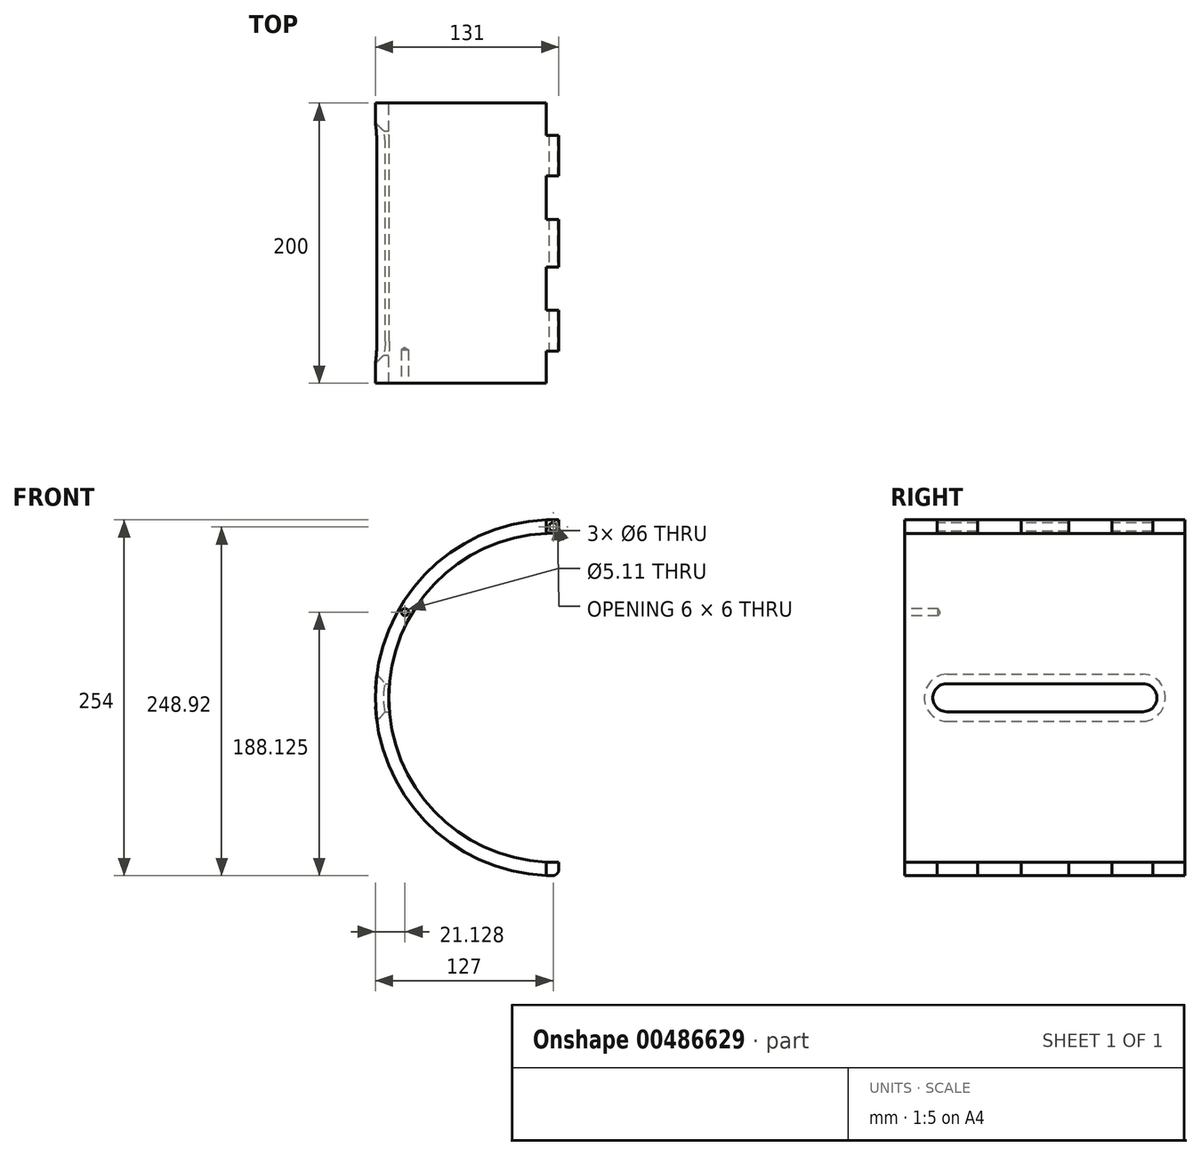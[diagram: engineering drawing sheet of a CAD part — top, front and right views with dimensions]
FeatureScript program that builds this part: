
annotation { "Feature Type Name" : "Feature", "Feature Type Description" : "" }
export const myFeature = defineFeature(function(context is Context, id is Id, definition is map)
    precondition{}
    {
        {
            var Q0;
            Q0=qCreatedBy(makeId("Front.planeOp"),FACE);
            var sketch = newSketch(context, id + "F0", { "sketchPlane" : qUnion([Q0])});
            skCircle(sketch, "E0", {"center": v(0, 0) * mm, "radius": 117.42 * mm});
            skCircle(sketch, "E1", {"center": v(0, 0) * mm, "radius": 127 * mm});
            skSolve(sketch);
        }
        {
            var Q0;
            Q0=makeQuery(id+"F0.imprint","IMPRINT",FACE,{"disambiguationData":[TD([[makeQuery(id+"F0.imprint","IMPRINT",EDGE,{"derivedFrom":sQuery(id+"F0.wireOp",EDGE,"E0")}),-1.0]])]});
            extrude(context, id + "F1", {"entities" : qUnion([Q0]), "endBound" : BoundingType.SYMMETRIC, "depth" : 200 * mm});
        }
        {
            var Q0;
            Q0=qCreatedBy(makeId("Front.planeOp"),FACE);
            var sketch = newSketch(context, id + "F2", { "sketchPlane" : qUnion([Q0])});
            skLineSegment(sketch, "E2", {"start": v(0, 0) * mm, "end": v(0, 160.57) * mm, "construction": true});
            skSolve(sketch);
        }
        {
            var Q0;
            Q0=makeQuery(id+"F1.opExtrude","CAP_FACE",FACE,{"disambiguationData":[OSD([sQuery(id+"F0.wireOp",EDGE,"E0"),sQuery(id+"F0.wireOp",EDGE,"E1")])],"isStart":false});
            var sketch = newSketch(context, id + "F3", { "sketchPlane" : qUnion([Q0])});
            skCircle(sketch, "E3", {"center": v(0, 121.92) * mm, "radius": 3 * mm});
            skSolve(sketch);
        }
        {
            var Q0;
            Q0=makeQuery(id+"F3.imprint","IMPRINT",FACE,{"disambiguationData":[TD([[makeQuery(id+"F3.imprint","IMPRINT",EDGE,{"derivedFrom":sQuery(id+"F3.wireOp",EDGE,"E3")}),1.0]])]});
            extrude(context, id + "F4", {"entities" : qUnion([Q0]), "operationType" : NewBodyOperationType.REMOVE, "endBound" : BoundingType.THROUGH_ALL, "oppositeDirection" : true, "depth" : 25 * mm});
        }
        {
            var Q0;
            Q0=qCreatedBy(makeId("Top.planeOp"),FACE);
            var sketch = newSketch(context, id + "F5", { "sketchPlane" : qUnion([Q0])});
            skLineSegment(sketch, "E4", {"start": v(0, 100.89) * mm, "end": v(0, -112.88) * mm, "construction": true});
            skLineSegment(sketch, "E5", {"start": v(-85.43, 0) * mm, "end": v(71.36, 0) * mm, "construction": true});
            skLineSegment(sketch, "E6", {"start": v(4, 77) * mm, "end": v(4, 48) * mm});
            skLineSegment(sketch, "E7.0", {"start": v(-5, 104.48) * mm, "end": v(-5, 77) * mm});
            skLineSegment(sketch, "E8.0", {"start": v(-5, 48) * mm, "end": v(-5, 17) * mm});
            skLineSegment(sketch, "E9.0", {"start": v(4, 48) * mm, "end": v(-5, 48) * mm});
            skLineSegment(sketch, "E10", {"start": v(-5, 17) * mm, "end": v(4, 17) * mm});
            skPoint(sketch, "E11.orphan", {"position": v(-5, 17.5) * mm});
            skLineSegment(sketch, "E12.MirrorCS", {"start": v(-5, -17) * mm, "end": v(4, -17) * mm});
            skLineSegment(sketch, "E13.MirrorCS", {"start": v(4, -48) * mm, "end": v(-5, -48) * mm});
            skLineSegment(sketch, "E14.MirrorCS", {"start": v(-5, -48) * mm, "end": v(-5, -17) * mm});
            skLineSegment(sketch, "E15.MirrorCS", {"start": v(-5, -104.48) * mm, "end": v(-5, -77) * mm});
            skLineSegment(sketch, "E16.MirrorCS", {"start": v(-5, -77) * mm, "end": v(4, -77) * mm});
            skLineSegment(sketch, "E17.MirrorCS", {"start": v(4, -77) * mm, "end": v(4, -48) * mm});
            skLineSegment(sketch, "E18", {"start": v(-5, 77) * mm, "end": v(4, 77) * mm});
            skLineSegment(sketch, "E19", {"start": v(4, -17) * mm, "end": v(4, 17) * mm});
            skLineSegment(sketch, "E20", {"start": v(-5, -104.48) * mm, "end": v(139.16, -104.48) * mm});
            skLineSegment(sketch, "E21", {"start": v(139.16, -104.48) * mm, "end": v(139.16, 104.48) * mm});
            skLineSegment(sketch, "E22", {"start": v(139.16, 104.48) * mm, "end": v(-5, 104.48) * mm});
            skSolve(sketch);
        }
        {
            var Q0;
            Q0=makeQuery(id+"F5.imprint","IMPRINT",FACE,{"disambiguationData":[TD([[makeQuery(id+"F5.imprint","IMPRINT",EDGE,{"derivedFrom":sQuery(id+"F5.wireOp",EDGE,"E6")}),1.0]])]});
            extrude(context, id + "F6", {"entities" : qUnion([Q0]), "operationType" : NewBodyOperationType.REMOVE, "endBound" : BoundingType.SYMMETRIC, "oppositeDirection" : true, "depth" : 300 * mm});
        }
        {
            var Q0;
            Q0=makeQuery(id+"F6.boolean.opBoolean","INTERSECT",EDGE,{"disambiguationData":[OD(0.0)],"derivedFrom":[makeQuery(id+"F1.opExtrude","SWEPT_FACE",FACE,{"disambiguationData":[OSD([sQuery(id+"F0.wireOp",EDGE,"E1")])]}),makeQuery(id+"F6.opExtrude","SWEPT_FACE",FACE,{"disambiguationData":[OSD([sQuery(id+"F5.wireOp",EDGE,"E17.MirrorCS")])]})]});
            var Q1;
            Q1=makeQuery(id+"F6.boolean.opBoolean","INTERSECT",EDGE,{"disambiguationData":[OD(0.0)],"derivedFrom":[makeQuery(id+"F1.opExtrude","SWEPT_FACE",FACE,{"disambiguationData":[OSD([sQuery(id+"F0.wireOp",EDGE,"E1")])]}),makeQuery(id+"F6.opExtrude","SWEPT_FACE",FACE,{"disambiguationData":[OSD([sQuery(id+"F5.wireOp",EDGE,"E19")])]})]});
            var Q2;
            Q2=makeQuery(id+"F6.boolean.opBoolean","INTERSECT",EDGE,{"disambiguationData":[OD(0.0)],"derivedFrom":[makeQuery(id+"F1.opExtrude","SWEPT_FACE",FACE,{"disambiguationData":[OSD([sQuery(id+"F0.wireOp",EDGE,"E1")])]}),makeQuery(id+"F6.opExtrude","SWEPT_FACE",FACE,{"disambiguationData":[OSD([sQuery(id+"F5.wireOp",EDGE,"E6")])]})]});
            fillet(context, id + "F7", {"entities" : qUnion([Q0, Q1, Q2]), "radius" : 4.5 * mm, "tangentPropagation" : true, "allowEdgeOverflow" : false});
        }
        {
            var Q0;
            Q0=qCreatedBy(makeId("Right.planeOp"),FACE);
            var sketch = newSketch(context, id + "F8", { "sketchPlane" : qUnion([Q0])});
            skLineSegment(sketch, "E23", {"start": v(-123.75, 0) * mm, "end": v(112.08, 0) * mm, "construction": true});
            skArc(sketch, "E24", {"start": v(-70, 10) * mm, "mid": v(-80, 0) * mm, "end": v(-70, -10) * mm});
            skArc(sketch, "E25", {"start": v(70, -10) * mm, "mid": v(80, 0) * mm, "end": v(70, 10) * mm});
            skLineSegment(sketch, "E26", {"start": v(-70, 10) * mm, "end": v(70, 10) * mm});
            skLineSegment(sketch, "E27", {"start": v(-70, -10) * mm, "end": v(70, -10) * mm});
            skSolve(sketch);
        }
        {
            var Q0;
            Q0=makeQuery(id+"F8.imprint","IMPRINT",FACE,{"disambiguationData":[TD([[makeQuery(id+"F8.imprint","IMPRINT",EDGE,{"derivedFrom":sQuery(id+"F8.wireOp",EDGE,"E24")}),1.0]])]});
            extrude(context, id + "F9", {"entities" : qUnion([Q0]), "operationType" : NewBodyOperationType.REMOVE, "oppositeDirection" : true, "depth" : 300 * mm});
        }
        {
            var Q0;
            Q0=makeQuery(id+"F9.boolean.opBoolean","INTERSECT",EDGE,{"derivedFrom":[makeQuery(id+"F1.opExtrude","SWEPT_FACE",FACE,{"disambiguationData":[OSD([sQuery(id+"F0.wireOp",EDGE,"E1")])]}),makeQuery(id+"F9.opExtrude","SWEPT_FACE",FACE,{"disambiguationData":[OSD([sQuery(id+"F8.wireOp",EDGE,"E27")])]})]});
            var Q1;
            Q1=makeQuery(id+"F9.boolean.opBoolean","INTERSECT",EDGE,{"derivedFrom":[makeQuery(id+"F1.opExtrude","SWEPT_FACE",FACE,{"disambiguationData":[OSD([sQuery(id+"F0.wireOp",EDGE,"E1")])]}),makeQuery(id+"F9.opExtrude","SWEPT_FACE",FACE,{"disambiguationData":[OSD([sQuery(id+"F8.wireOp",EDGE,"E25")])]})]});
            var Q2;
            Q2=makeQuery(id+"F9.boolean.opBoolean","INTERSECT",EDGE,{"derivedFrom":[makeQuery(id+"F1.opExtrude","SWEPT_FACE",FACE,{"disambiguationData":[OSD([sQuery(id+"F0.wireOp",EDGE,"E1")])]}),makeQuery(id+"F9.opExtrude","SWEPT_FACE",FACE,{"disambiguationData":[OSD([sQuery(id+"F8.wireOp",EDGE,"E26")])]})]});
            chamfer(context, id + "F10", {"entities" : qUnion([Q0, Q1, Q2]), "width" : 6 * mm, "tangentPropagation" : true});
        }
        {
            var Q0;
            Q0=makeQuery(id+"F1.opExtrude","CAP_FACE",FACE,{"disambiguationData":[OSD([sQuery(id+"F0.wireOp",EDGE,"E0"),sQuery(id+"F0.wireOp",EDGE,"E1")])],"isStart":false});
            var sketch = newSketch(context, id + "F11", { "sketchPlane" : qUnion([Q0])});
            skLineSegment(sketch, "E28", {"start": v(-132.07, 0) * mm, "end": v(-112.46, 0) * mm, "construction": true});
            skPoint(sketch, "E28.endSnap0", {"position": v(-117.42, 0) * mm});
            skCircle(sketch, "E29", {"center": v(0, 0) * mm, "radius": 122.25 * mm, "construction": true});
            skLineSegment(sketch, "E30", {"start": v(0, 0) * mm, "end": v(-109.99, 63.5) * mm, "construction": true});
            skPoint(sketch, "E31", {"position": v(-105.87, 61.12) * mm});
            skSolve(sketch);
        }
        {
            var Q0;
            Q0=sQuery(id+"F11.wireOp",VERTEX,"E31");
            var Q1;
            Q1=makeQuery(id+"F1.opExtrude","SWEPT_BODY",BODY,{"disambiguationData":[OSD([sQuery(id+"F0.wireOp",EDGE,"E0"),sQuery(id+"F0.wireOp",EDGE,"E1")])]});
            hole(context, id + "F12", {"style" : HoleStyle.SIMPLE, "endStyle" : HoleEndStyle.BLIND, "standardTappedOrClearance" : lookupTablePath({ "standard" : "ANSI", "engagement" : "75%", "pitch" : "20 tpi", "size" : "1/4", "type" : "Tapped" }), "standardBlindInLast" : lookupTablePath({ "standard" : "ANSI", "engagement" : "75%", "pitch" : "20 tpi", "size" : "1/4", "type" : "Tapped" }), "holeDiameter" : 5.1 * mm, "showTappedDepth" : true, "holeDepth" : 23.8 * mm, "isTappedThrough" : true, "tappedDepth" : 20 * mm, "tapClearance" : 3, "startFromSketch" : true, "locations" : qUnion([Q0]), "scope" : qUnion([Q1]), "majorDiameter" : 6.35 * mm});
        }
    });
